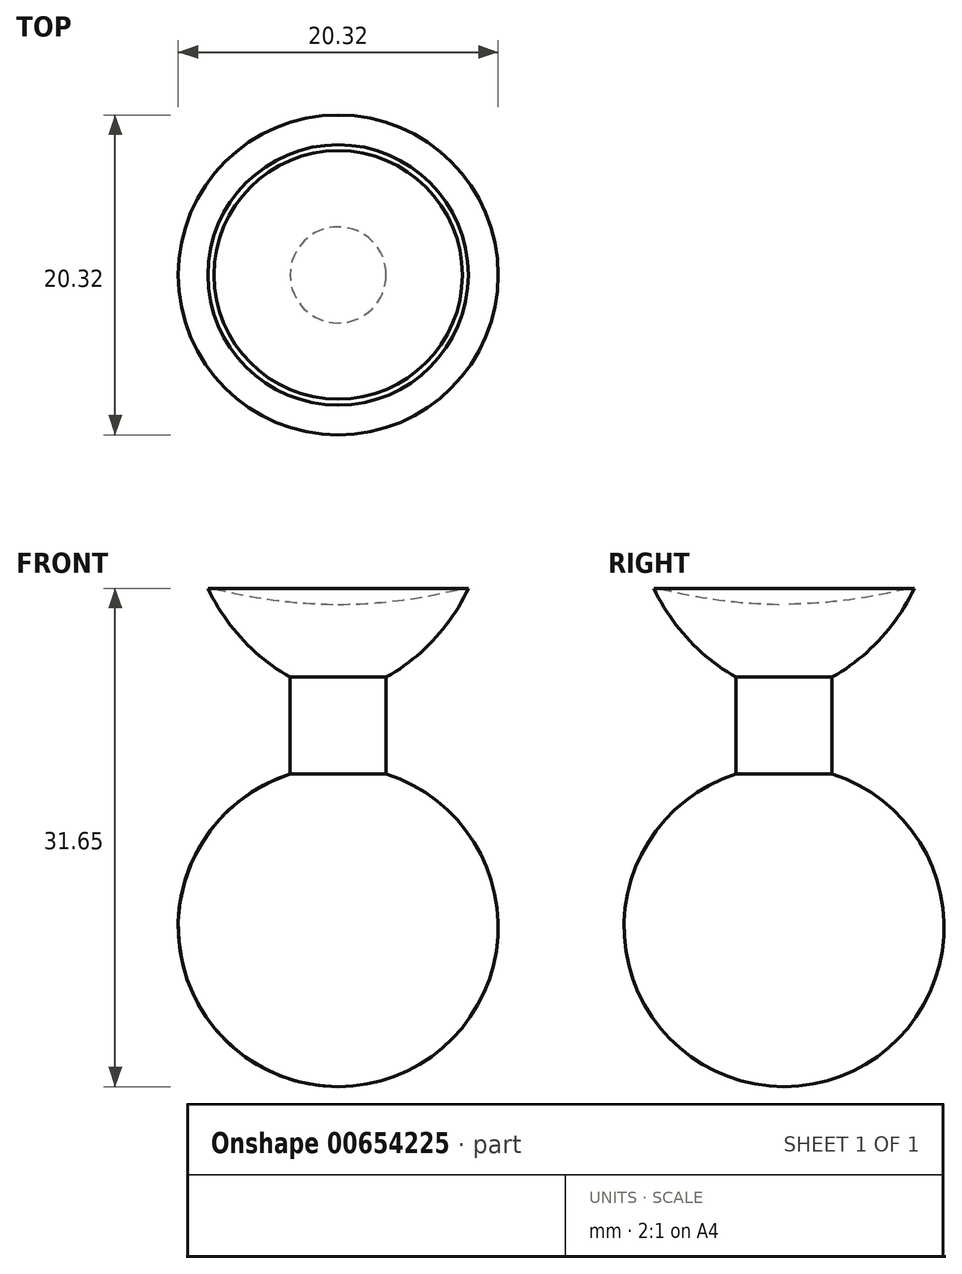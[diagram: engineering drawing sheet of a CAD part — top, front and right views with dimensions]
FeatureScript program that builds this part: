
annotation { "Feature Type Name" : "Feature", "Feature Type Description" : "" }
export const myFeature = defineFeature(function(context is Context, id is Id, definition is map)
    precondition{}
    {
        {
            var Q0;
            Q0=qCreatedBy(makeId("Front.planeOp"),FACE);
            var sketch = newSketch(context, id + "F0", { "sketchPlane" : qUnion([Q0])});
            skLineSegment(sketch, "E0", {"start": v(0, 0) * mm, "end": v(0, 20.32) * mm});
            skArc(sketch, "E1", {"start": v(0, 20.32) * mm, "mid": v(-10.16, 10.16) * mm, "end": v(0, 0) * mm});
            skPoint(sketch, "E2.orphan", {"position": v(0, 40.64) * mm});
            skLineSegment(sketch, "E3", {"start": v(0, 20.32) * mm, "end": v(0, 24.77) * mm});
            skArc(sketch, "E4", {"start": v(-8.27, 31.65) * mm, "mid": v(-4.9, 27.29) * mm, "end": v(0, 24.77) * mm});
            skLineSegment(sketch, "E5", {"start": v(-8.27, 31.65) * mm, "end": v(-7.89, 31.65) * mm});
            skLineSegment(sketch, "E6", {"start": v(0, 30.63) * mm, "end": v(0, 24.77) * mm});
            skArc(sketch, "E7", {"start": v(-7.89, 31.65) * mm, "mid": v(-3.98, 30.9) * mm, "end": v(0, 30.63) * mm});
            skLineSegment(sketch, "E8", {"start": v(-3.05, 26) * mm, "end": v(-3.05, 19.85) * mm});
            skSolve(sketch);
        }
        {
            var Q0;
            {var subQ0=sQuery(id+"F0.wireOp",EDGE,"E0");Q0=makeQuery(id+"F0.imprint","IMPRINT",FACE,{"disambiguationData":[TD([[makeQuery(id+"F0.imprint","IMPRINT",EDGE,{"derivedFrom":subQ0}),1.0]])]});}
            var Q1;
            {var subQ0=sQuery(id+"F0.wireOp",EDGE,"E3");Q1=makeQuery(id+"F0.imprint","IMPRINT",FACE,{"disambiguationData":[TD([[makeQuery(id+"F0.imprint","IMPRINT",EDGE,{"derivedFrom":subQ0}),1.0]])]});}
            var Q2;
            {var subQ1=sQuery(id+"F0.wireOp",EDGE,"E5");Q2=makeQuery(id+"F0.imprint","IMPRINT",FACE,{"disambiguationData":[TD([[makeQuery(id+"F0.imprint","IMPRINT",EDGE,{"derivedFrom":subQ1}),-1.0]])]});}
            var Q3;
            Q3=sQuery(id+"F0.wireOp",EDGE,"E0");
            revolve(context, id + "F1", {"entities" : qUnion([Q0, Q1, Q2]), "axis" : qUnion([Q3]), "revolveType" : RevolveType.FULL});
        }
    });
